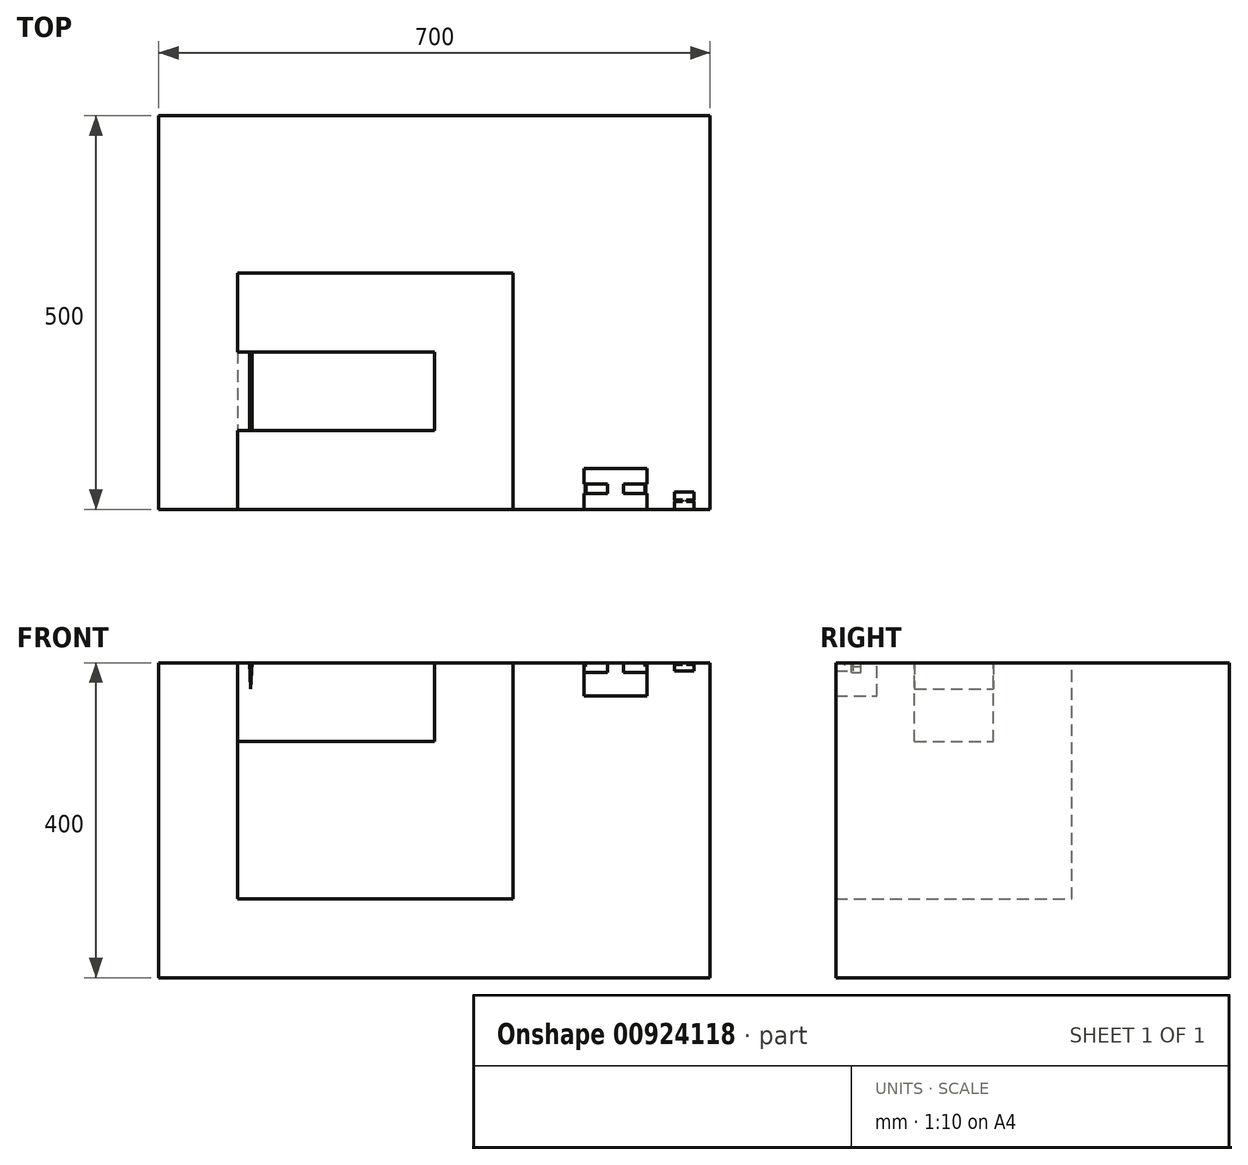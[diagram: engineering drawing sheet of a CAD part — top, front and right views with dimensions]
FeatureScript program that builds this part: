
annotation { "Feature Type Name" : "Feature", "Feature Type Description" : "" }
export const myFeature = defineFeature(function(context is Context, id is Id, definition is map)
    precondition{}
    {
        {
            var Q0;
            Q0=qCreatedBy(makeId("Top.planeOp"),FACE);
            var sketch = newSketch(context, id + "F0", { "sketchPlane" : qUnion([Q0])});
            skLineSegment(sketch, "E0.bottom", {"start": v(350, 250) * mm, "end": v(-350, 250) * mm});
            skLineSegment(sketch, "E0.top", {"start": v(350, -250) * mm, "end": v(-350, -250) * mm});
            skLineSegment(sketch, "E0.left", {"start": v(350, 250) * mm, "end": v(350, -250) * mm});
            skLineSegment(sketch, "E0.right", {"start": v(-350, 250) * mm, "end": v(-350, -250) * mm});
            skPoint(sketch, "E0.middle", {"position": v(0, 0) * mm});
            skSolve(sketch);
        }
        {
            var Q0;
            Q0=makeQuery(id+"F0.imprint","IMPRINT",FACE,{"disambiguationData":[TD([[makeQuery(id+"F0.imprint","IMPRINT",EDGE,{"derivedFrom":sQuery(id+"F0.wireOp",EDGE,"E0.bottom")}),1.0]])]});
            var Q1;
            Q1 = qSketchRegion(id + "F2", true);
            extrude(context, id + "F1", {"entities" : qUnion([Q0, Q1]), "depth" : 400 * mm, "offsetDistance" : 25.4 * mm});
        }
        {
            var Q0;
            Q0=makeQuery(id+"F1.opExtrude","CAP_FACE",FACE,{"disambiguationData":[OSD([sQuery(id+"F0.wireOp",EDGE,"E0.bottom"),sQuery(id+"F0.wireOp",EDGE,"E0.top"),sQuery(id+"F0.wireOp",EDGE,"E0.left"),sQuery(id+"F0.wireOp",EDGE,"E0.right")])],"isStart":false});
            var sketch = newSketch(context, id + "F2", { "sketchPlane" : qUnion([Q0])});
            skLineSegment(sketch, "E1.bottom", {"start": v(305, -250) * mm, "end": v(330, -250) * mm});
            skLineSegment(sketch, "E1.top", {"start": v(305, -228) * mm, "end": v(330, -228) * mm});
            skLineSegment(sketch, "E1.left", {"start": v(305, -250) * mm, "end": v(305, -228) * mm});
            skLineSegment(sketch, "E1.right", {"start": v(330, -250) * mm, "end": v(330, -228) * mm});
            skLineSegment(sketch, "E2.bottom", {"start": v(305, -240) * mm, "end": v(315, -240) * mm});
            skLineSegment(sketch, "E2.top", {"start": v(305, -238) * mm, "end": v(315, -238) * mm});
            skLineSegment(sketch, "E2.left", {"start": v(305, -240) * mm, "end": v(305, -238) * mm});
            skLineSegment(sketch, "E2.right", {"start": v(315, -240) * mm, "end": v(315, -238) * mm});
            skLineSegment(sketch, "E3.bottom", {"start": v(330, -240) * mm, "end": v(320, -240) * mm});
            skLineSegment(sketch, "E3.top", {"start": v(330, -238) * mm, "end": v(320, -238) * mm});
            skLineSegment(sketch, "E3.left", {"start": v(330, -240) * mm, "end": v(330, -238) * mm});
            skLineSegment(sketch, "E3.right", {"start": v(320, -240) * mm, "end": v(320, -238) * mm});
            skLineSegment(sketch, "E4.bottom", {"start": v(270, -250) * mm, "end": v(190, -250) * mm});
            skLineSegment(sketch, "E4.top", {"start": v(270, -198) * mm, "end": v(190, -198) * mm});
            skLineSegment(sketch, "E4.left", {"start": v(270, -250) * mm, "end": v(270, -198) * mm});
            skLineSegment(sketch, "E4.right", {"start": v(190, -250) * mm, "end": v(190, -198) * mm});
            skLineSegment(sketch, "E5.bottom", {"start": v(190, -230) * mm, "end": v(220, -230) * mm});
            skLineSegment(sketch, "E5.top", {"start": v(190, -218) * mm, "end": v(220, -218) * mm});
            skLineSegment(sketch, "E5.left", {"start": v(190, -230) * mm, "end": v(190, -218) * mm});
            skLineSegment(sketch, "E5.right", {"start": v(220, -230) * mm, "end": v(220, -218) * mm});
            skLineSegment(sketch, "E6.bottom", {"start": v(270, -230) * mm, "end": v(240, -230) * mm});
            skLineSegment(sketch, "E6.top", {"start": v(270, -218) * mm, "end": v(240, -218) * mm});
            skLineSegment(sketch, "E6.left", {"start": v(270, -230) * mm, "end": v(270, -218) * mm});
            skLineSegment(sketch, "E6.right", {"start": v(240, -230) * mm, "end": v(240, -218) * mm});
            skLineSegment(sketch, "E7.bottom", {"start": v(100, -250) * mm, "end": v(-250, -250) * mm});
            skLineSegment(sketch, "E7.top", {"start": v(100, 50) * mm, "end": v(-250, 50) * mm});
            skLineSegment(sketch, "E7.left", {"start": v(100, -250) * mm, "end": v(100, 50) * mm});
            skLineSegment(sketch, "E7.right", {"start": v(-250, -250) * mm, "end": v(-250, 50) * mm});
            skLineSegment(sketch, "E8.bottom", {"start": v(-250, -150) * mm, "end": v(0, -150) * mm});
            skLineSegment(sketch, "E8.top", {"start": v(-250, -50) * mm, "end": v(0, -50) * mm});
            skLineSegment(sketch, "E8.left", {"start": v(-250, -150) * mm, "end": v(-250, -50) * mm});
            skLineSegment(sketch, "E8.right", {"start": v(0, -150) * mm, "end": v(0, -50) * mm});
            skLineSegment(sketch, "E9.bottom", {"start": v(0, -150) * mm, "end": v(100, -150) * mm});
            skLineSegment(sketch, "E9.top", {"start": v(0, -50) * mm, "end": v(100, -50) * mm});
            skLineSegment(sketch, "E9.right", {"start": v(100, -150) * mm, "end": v(100, -50) * mm});
            skSolve(sketch);
        }
        {
            var Q0;
            {var subQ7=sQuery(id+"F2.wireOp",EDGE,"E1.bottom");Q0=makeQuery(id+"F2.imprint","IMPRINT",FACE,{"disambiguationData":[TD([[makeQuery(id+"F2.imprint","IMPRINT",EDGE,{"derivedFrom":subQ7}),-1.0]])]});}
            extrude(context, id + "F3", {"entities" : qUnion([Q0]), "operationType" : NewBodyOperationType.REMOVE, "oppositeDirection" : true, "depth" : 10 * mm, "offsetDistance" : 25 * mm});
        }
        {
            var Q0;
            {var subQ6=sQuery(id+"F2.wireOp",EDGE,"E4.bottom");Q0=makeQuery(id+"F2.imprint","IMPRINT",FACE,{"disambiguationData":[TD([[makeQuery(id+"F2.imprint","IMPRINT",EDGE,{"derivedFrom":subQ6}),-1.0]])]});}
            extrude(context, id + "F4", {"entities" : qUnion([Q0]), "operationType" : NewBodyOperationType.REMOVE, "depth" : -42 * mm, "offsetDistance" : 25 * mm});
        }
        {
            var Q0;
            {var subQ2=sQuery(id+"F2.wireOp",EDGE,"E7.top");Q0=makeQuery(id+"F2.imprint","IMPRINT",FACE,{"disambiguationData":[TD([[makeQuery(id+"F2.imprint","IMPRINT",EDGE,{"derivedFrom":subQ2}),1.0]])]});}
            var Q1;
            {var subQ2=sQuery(id+"F2.wireOp",EDGE,"E7.bottom");Q1=makeQuery(id+"F2.imprint","IMPRINT",FACE,{"disambiguationData":[TD([[makeQuery(id+"F2.imprint","IMPRINT",EDGE,{"derivedFrom":subQ2}),-1.0]])]});}
            var Q2;
            {var subQ5=sQuery(id+"F2.wireOp",EDGE,"3sNkvcZL-EcoH-w4F9-NcZa-U5I6iMzT4b8Z.bottom");Q2=makeQuery(id+"F2.imprint","IMPRINT",FACE,{"disambiguationData":[TD([[makeQuery(id+"F2.imprint","IMPRINT",EDGE,{"derivedFrom":subQ5}),1.0]])]});}
            var Q3;
            {var subQ5=sQuery(id+"F2.wireOp",EDGE,"3sNkvcZL-EcoH-w4F9-NcZa-U5I6iMzT4b8Z.top");Q3=makeQuery(id+"F2.imprint","IMPRINT",FACE,{"disambiguationData":[TD([[makeQuery(id+"F2.imprint","IMPRINT",EDGE,{"derivedFrom":subQ5}),-1.0]])]});}
            extrude(context, id + "F5", {"entities" : qUnion([Q0, Q1, Q2, Q3]), "operationType" : NewBodyOperationType.REMOVE, "oppositeDirection" : true, "depth" : 300 * mm, "offsetDistance" : 25 * mm});
        }
        {
            var Q0;
            Q0=makeQuery(id+"F2.imprint","IMPRINT",FACE,{"disambiguationData":[TD([[makeQuery(id+"F2.imprint","IMPRINT",EDGE,{"derivedFrom":sQuery(id+"F2.wireOp",EDGE,"E9.bottom")}),1.0]])]});
            extrude(context, id + "F6", {"entities" : qUnion([Q0]), "operationType" : NewBodyOperationType.REMOVE, "oppositeDirection" : true, "depth" : 300 * mm, "offsetDistance" : 25 * mm});
        }
        {
            var Q0;
            Q0=makeQuery(id+"F1.opExtrude","SWEPT_FACE",FACE,{"disambiguationData":[OSD([sQuery(id+"F0.wireOp",EDGE,"E0.top")])]});
            var sketch = newSketch(context, id + "F7", { "sketchPlane" : qUnion([Q0])});
            skLineSegment(sketch, "E10.bottom", {"start": v(305, 390) * mm, "end": v(330, 390) * mm});
            skLineSegment(sketch, "E10.top", {"start": v(305, 398) * mm, "end": v(330, 398) * mm});
            skLineSegment(sketch, "E10.left", {"start": v(305, 390) * mm, "end": v(305, 398) * mm});
            skLineSegment(sketch, "E10.right", {"start": v(330, 390) * mm, "end": v(330, 398) * mm});
            skLineSegment(sketch, "E11.bottom", {"start": v(190, 358) * mm, "end": v(270, 358) * mm});
            skLineSegment(sketch, "E11.top", {"start": v(190, 388) * mm, "end": v(270, 388) * mm});
            skLineSegment(sketch, "E11.left", {"start": v(190, 358) * mm, "end": v(190, 388) * mm});
            skLineSegment(sketch, "E11.right", {"start": v(270, 358) * mm, "end": v(270, 388) * mm});
            skLineSegment(sketch, "E12.bottom", {"start": v(-250, 100) * mm, "end": v(100, 100) * mm});
            skLineSegment(sketch, "E12.top", {"start": v(-250, 300) * mm, "end": v(100, 300) * mm});
            skLineSegment(sketch, "E12.left", {"start": v(-250, 100) * mm, "end": v(-250, 300) * mm});
            skLineSegment(sketch, "E12.right", {"start": v(100, 100) * mm, "end": v(100, 300) * mm});
            skSolve(sketch);
        }
        {
            var Q0;
            Q0=makeQuery(id+"F7.imprint","IMPRINT",FACE,{"disambiguationData":[TD([[makeQuery(id+"F7.imprint","IMPRINT",EDGE,{"derivedFrom":sQuery(id+"F7.wireOp",EDGE,"E10.bottom")}),-1.0]])]});
            extrude(context, id + "F8", {"entities" : qUnion([Q0]), "operationType" : NewBodyOperationType.REMOVE, "oppositeDirection" : true, "depth" : 22 * mm, "offsetDistance" : 25 * mm});
        }
        {
            var Q0;
            Q0=makeQuery(id+"F7.imprint","IMPRINT",FACE,{"disambiguationData":[TD([[makeQuery(id+"F7.imprint","IMPRINT",EDGE,{"derivedFrom":sQuery(id+"F7.wireOp",EDGE,"E11.bottom")}),-1.0]])]});
            extrude(context, id + "F9", {"entities" : qUnion([Q0]), "operationType" : NewBodyOperationType.REMOVE, "oppositeDirection" : true, "depth" : 42 * mm, "offsetDistance" : 25 * mm});
        }
        {
            var Q0;
            Q0=makeQuery(id+"F7.imprint","IMPRINT",FACE,{"disambiguationData":[TD([[makeQuery(id+"F7.imprint","IMPRINT",EDGE,{"derivedFrom":sQuery(id+"F7.wireOp",EDGE,"E12.bottom")}),-1.0]])]});
            extrude(context, id + "F10", {"entities" : qUnion([Q0]), "operationType" : NewBodyOperationType.REMOVE, "oppositeDirection" : true, "depth" : 300 * mm, "offsetDistance" : 25 * mm});
        }
        {
            var Q0;
            {var subQ20=sQuery(id+"F2.wireOp",EDGE,"E1.top");Q0=makeQuery(id+"F2.imprint","IMPRINT",FACE,{"disambiguationData":[TD([[makeQuery(id+"F2.imprint","IMPRINT",EDGE,{"derivedFrom":subQ20}),1.0]])]});}
            var sketch = newSketch(context, id + "F11", { "sketchPlane" : qUnion([Q0])});
            skLineSegment(sketch, "E13.bottom", {"start": v(-235, -156.95) * mm, "end": v(-231.5, -156.95) * mm});
            skLineSegment(sketch, "E13.top", {"start": v(-235, -36.95) * mm, "end": v(-231.5, -36.95) * mm});
            skLineSegment(sketch, "E13.left", {"start": v(-235, -156.95) * mm, "end": v(-235, -36.95) * mm});
            skLineSegment(sketch, "E13.right", {"start": v(-231.5, -156.95) * mm, "end": v(-231.5, -36.95) * mm});
            skLineSegment(sketch, "E14.bottom", {"start": v(192, -215.65) * mm, "end": v(192.5, -215.65) * mm});
            skLineSegment(sketch, "E14.top", {"start": v(192, -235.65) * mm, "end": v(192.5, -235.65) * mm});
            skLineSegment(sketch, "E14.left", {"start": v(192, -215.65) * mm, "end": v(192, -235.65) * mm});
            skLineSegment(sketch, "E14.right", {"start": v(192.5, -215.65) * mm, "end": v(192.5, -235.65) * mm});
            skLineSegment(sketch, "E15.bottom", {"start": v(267.5, -213.45) * mm, "end": v(268, -213.45) * mm});
            skLineSegment(sketch, "E15.top", {"start": v(267.5, -233.45) * mm, "end": v(268, -233.45) * mm});
            skLineSegment(sketch, "E15.left", {"start": v(267.5, -213.45) * mm, "end": v(267.5, -233.45) * mm});
            skLineSegment(sketch, "E15.right", {"start": v(268, -213.45) * mm, "end": v(268, -233.45) * mm});
            skLineSegment(sketch, "E16.bottom", {"start": v(305.75, -237.16) * mm, "end": v(305.85, -237.16) * mm});
            skLineSegment(sketch, "E16.top", {"start": v(305.75, -241.04) * mm, "end": v(305.85, -241.04) * mm});
            skLineSegment(sketch, "E16.left", {"start": v(305.75, -237.16) * mm, "end": v(305.75, -241.04) * mm});
            skLineSegment(sketch, "E16.right", {"start": v(305.85, -237.16) * mm, "end": v(305.85, -241.04) * mm});
            skLineSegment(sketch, "E17.bottom", {"start": v(329.15, -237.16) * mm, "end": v(329.25, -237.16) * mm});
            skLineSegment(sketch, "E17.top", {"start": v(329.15, -241.04) * mm, "end": v(329.25, -241.04) * mm});
            skLineSegment(sketch, "E17.left", {"start": v(329.15, -237.16) * mm, "end": v(329.15, -241.04) * mm});
            skLineSegment(sketch, "E17.right", {"start": v(329.25, -237.16) * mm, "end": v(329.25, -241.04) * mm});
            skSolve(sketch);
        }
        {
            var Q0;
            Q0 = qSketchRegion(id + "F11", true);
            var Q1;
            Q1=sQuery(id+"F2.wireOp",EDGE,"3sNkvcZL-EcoH-w4F9-NcZa-U5I6iMzT4b8Z.left");
            extrude(context, id + "F12", {"entities" : qUnion([Q0]), "operationType" : NewBodyOperationType.REMOVE, "surfaceEntities" : qUnion([Q1]), "oppositeDirection" : true, "depth" : 33 * mm, "offsetDistance" : 25 * mm, "hasDraft" : true, "draftAngle" : 3 * degree, "draftPullDirection" : true});
        }
    });
